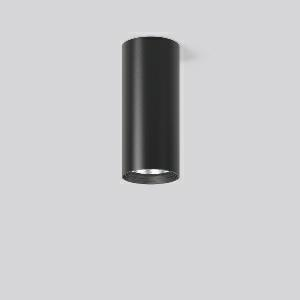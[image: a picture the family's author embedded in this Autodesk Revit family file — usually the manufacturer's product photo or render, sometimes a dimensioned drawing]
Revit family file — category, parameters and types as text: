
# Revit family: heledon_mini_a_931200_003_1_3d29
name_source: partatom
category: Lighting Fixtures
units: mm (PartAtom-declared; Revit-internal decimal feet)

## family parameters
Cut with Voids When Loaded = No
Host = Face
Light Source = No
Part Type = Normal
Room Calculation Point = No
Round Connector Dimension = Use Diameter
Shared = No

## types (1)
- HELEDON mini A (1 x LED Modul 940, 2700 lm, 4000)
    Apparent Load = 20 VA
    Approval mark = CE
    CIE Flux Codes = 100 100 100 100 100
    Color Rendering = 92
    Color Temperature = 4000
    Default Elevation = 1800 mm
    Description = Series: HELEDON mini
Cylindrical surface-mounted downlight. Housing: die-cast aluminium, powder-coated. Internal ceiling frame polycarbonate with bayonet mounting. Black plastic ring and recessed LED to prevent glare from the side. Optical assembly with reflector made of MIRO-Silver with 98% total light reflection for outstanding efficiency - can be changed without tools. Best colour rendering index Ra>90. Suitable for Ceiling mounting. Easy installation with a separate ceiling frame with bayonet mounting and plug connection. Driver integrated. Connected via plug-in connector. High quality converter without flickering and stroboscopic effect. The following accessories can be mounted without use of tools: interchangeable lenses, decorative glasses, honeycomb louvre, clear and frosted diffusers, white interchangeable plastic ring. 
Colour: deep black, matt (RAL 9005)
Diameter: 87 mm
Height: 197 mm
Lamp: LED
Socket: without socket
Colour temperature: 4000K
Colour rendering index (CRI): 92
System power: 20 W
Rated luminous flux: 2700 lm
Luminous efficiency: 135 lm/W
Control gear: Regulated power supply
Protection class: I
Type of protection: IP 20
    Height = 197 mm
    Lamp = 1 x LED Modul 940
    Lamp Light Flux = 2700 lm
    Lamp count = 1
    Length = 87 mm
    Lifetime = 50000 h
    Luminous efficacy = 135 lm/W
    Manufacturer = RZB
    ModVariant = No
    Model = 931200.003.1
    Mounting Place = Ceiling
    Mounting Type = Surface mounted
    Number of Poles = 1
    OnlyDefault = Yes
    Power Factor = 1
    Product Name = HELEDON mini A
    Product group = Surface mounted downlights
    ProductGroupID = 302
    Protection Class = Protection class I
    Protection Degree = IP 20
    RLX_Detail_Level = 1
    RLX_Emergency_Light_Flux = 0 lm
    RLX_Emergency_Type = 0
    RLX_Emergency_Type_DB = No
    RlxData = <blob elided: 108037 chars, md5=1c40d6bc>
    Socket = socket
    Standby Power = 0 W
    System Light Flux = 2700 lm
    System Power = 20 W
    Type Comments = Product without accessories
    Type Image = 931188.003.jpg
    URL = http://relux.com
    VarID = ---
    Voltage = 230 V
    Voltage Range = 220-240 V
    Weight = 0.00 kg
    Width = 0 mm  [stored 0 ft]

note: [stored X ft] marks values corroborated as IEEE doubles in the binary element streams (Revit-internal decimal feet)

## geometry (parser evidence)
native form markers: Blend x4, Sweep x9
no freeform markers — native parametric forms only
